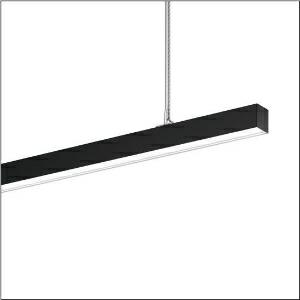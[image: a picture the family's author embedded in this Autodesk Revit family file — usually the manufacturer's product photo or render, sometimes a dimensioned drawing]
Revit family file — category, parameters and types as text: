
# Revit family: silica_r__21_51mx30da34bb_31c6
name_source: partatom
category: Lighting Fixtures
units: mm (PartAtom-declared; Revit-internal decimal feet)

## family parameters
Cut with Voids When Loaded = No
Host = Face
Light Source = No
Part Type = Normal
Room Calculation Point = No
Round Connector Dimension = Use Diameter
Shared = No

## types (1)
- --- (1 x LED, 4210 lm, 27.7 W, 3000K)
    Apparent Load = 28 VA
    CIE Flux Codes = 47 79 96 57 100
    Color Rendering = 80
    Color Temperature = 3000K
    Default Elevation = 1800 mm
    Description = Silica® 21, office luminaire, primary optical cover: cover, of PMMA, opal, light emission: direct/indirect distribution, primary light characteristic: symmetric, installation type: suspended mounting, LED, rated luminous flux: 4.210lm, luminous efficacy: 152lm/W, light colour: 830, colour temperature: 3000K, with terminal, 3+2-pole, max. 2.5mm², mains connection: 220..240V, AC, 50/60Hz, rated input power: 27.7W, luminaire housing, of aluminium, jet black (RAL 9005), length: 1.204mm, width: 53mm, height: 53mm, protection rating (complete): IP20, insulation class (complete): insulation class I (protective earthing), certification: CE, permissible operating ambient temperature: 0..+35°C, standard: EN 50419, packaging unit: 1 piece
    Height = 53 mm
    Lamp = 1 x LED
    Lamp Light Flux = 4210 lm
    Lamp Power = 27.7 W
    Lamp count = 1
    Length = 1204 mm
    Luminous efficacy = 152 lm/W
    Manufacturer = Siteco
    ModVariant = No
    Model = 51MX30DA34BB
    Mounting Place = Ceiling
    Mounting Type = Pendant
    Number of Poles = 1
    OnlyDefault = Yes
    Power Factor = 1
    Product Name = Silica® 21
    Product group = office luminaire | ceiling pendant
    ProductGroupID = 905
    Protection Class = Protection class I
    Protection Degree = IP 20
    RLX_Detail_Level = 1
    RlxData = <blob elided: 26017 chars, md5=0e99e0a6>
    Socket = socket
    Standby Power = 0 W
    System Light Flux = 4210 lm
    System Power = 28 W
    Type Comments = factory setting: luminous flux: 100 % | dim-lin: 254 | 233 mA
    Type Image = l_1251735.jpg
    URL = http://relux.com
    VarID = @adj_025713
    Voltage = 0 V
    Weight = 0.00 kg
    Width = 53 mm

## geometry (parser evidence)
native form markers: Blend x4, Sweep x13
no freeform markers — native parametric forms only
